# Revit family: Power-ModularDevices-GEWISS-90RCD-BD_2P
name_source: partatom
category: Apparecchi elettrici
revit_build: Autodesk Revit MEP 2016 (Build: 20150220_1215(x64)
units: mm (PartAtom-declared; Revit-internal decimal feet)

## family parameters
Condiviso = Sì
Host = Superficie
Mantenere orientamento annotazione = Sì
Numero OmniClass = 23.80.30.14
Punto di calcolo locali = Sì
Quota connettore circolare = Usa diametro
Taglio con vuoti quando caricato = No
Tipo di parte = Normale
Titolo OmniClass = Power Distribution

## types (1)
- Power-ModularDevices-GEWISS-90RCD-BD_2P
    Altezza = 92 mm
    Altezza pannello = 35 mm
    Assembly position: = Any
    Carico apparente = 0 VA
    Catalogue = POWER
    Catalogue Range = 90 RCD
    Description = RESIDUAL CURRENT DEVICE
    Descrizione = ADD-ON RCD 2P IN<63A IMMUN.A/0,03 2M
    EAN code = 8011564761971
    Electrocod = 1412
    Finitura = GW - grigio chiaro
    IDF = a2e4335f-66c0-4250-a404-7c4b8ea38134
    IDT = adf18db2-dbf0-4dcc-9ca3-3f3ec2ab55f8
    Idn = 30MA
    Immagine tipo = GW94401.jpg
    Insulation voltage = 500V
    Interuttore = GW - grigio scuro
    Label = BD
    Larghezza = 36 mm  [stored 0.11811 ft]
    Level of immunity (8/20 µs) = 3000A
    Modello = GW94566
    No. modules = 2
    No. of modules EN 50022 = 2
    No. of poles = 2P
    Number of poles = 2P
    Numero di poli_ = 2
    Operating temperature = -25 +40 °C
    Overvoltage category = III
    Parti incassate = Sì
    Precision = 30 mA
    Produttore = GEWISS S.p.A.
    Prospetto di default = 1219 mm
    Rated current (In) = 63A
    Rated current: = 63A
    Rated frequency (Hz) = 50/60 Hz
    Rated impulse withstand voltage = 4KV
    Rated insulation voltage (Ui) = 500V
    Rated residual operating current = 30 mA
    Rated tightening torque = 2 Nm
    Rated voltage = 230V
    Rated voltage (IEC/EN 61009-1 app. G, IEC/EN 61009-2-1 app. G) = 230V
    SEO = Add-on RCD
    Section flexible cable = Max 35 mm²
    Section rigid cable = Max 35 mm²
    Spessore = 65 mm
    Standard = EN 61009-1 app. G
    Standard; = IEC/EN 61009-1 app. G, IEC/EN 61009-2-1 app. G
    Stocking temperature = -40 +70 °C
    Technical sheet = https://www.gewiss.com
    Type = A(IR)
    Type: = A[IR]
    URL = https://www.gewiss.com
    Version file RFA = 19.0
    Voltaggio = 230 V

note: [stored X ft] marks values corroborated as IEEE doubles in the binary element streams (Revit-internal decimal feet)
